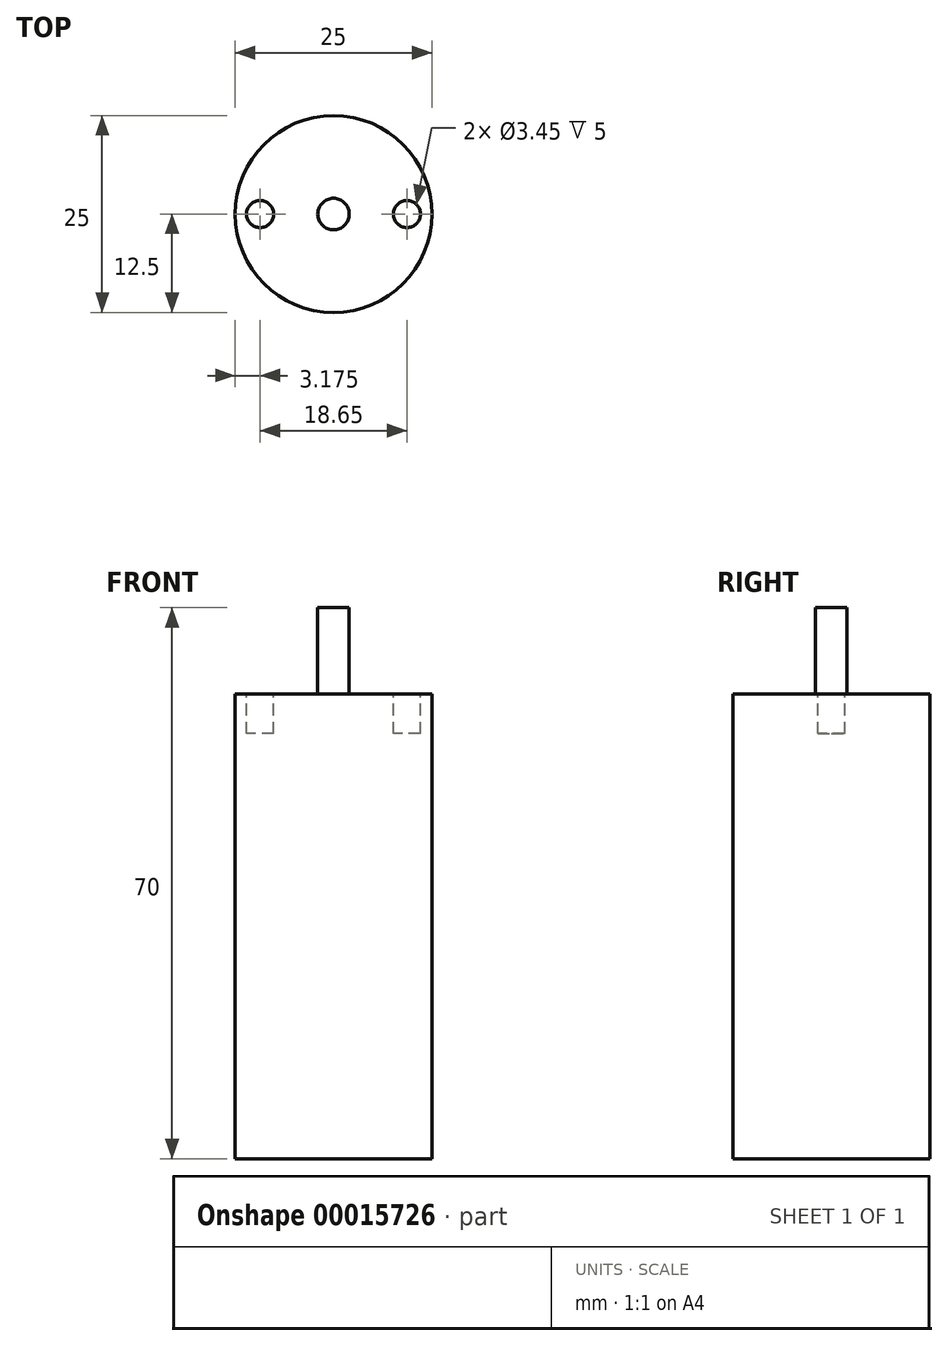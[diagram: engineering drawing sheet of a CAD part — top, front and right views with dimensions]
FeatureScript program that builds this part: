
annotation { "Feature Type Name" : "Feature", "Feature Type Description" : "" }
export const myFeature = defineFeature(function(context is Context, id is Id, definition is map)
    precondition{}
    {
        {
            var Q0;
            Q0=qCreatedBy(makeId("Top.planeOp"),FACE);
            var sketch = newSketch(context, id + "F0", { "sketchPlane" : qUnion([Q0])});
            skCircle(sketch, "E0", {"center": v(0, 0) * mm, "radius": 12.5 * mm});
            skSolve(sketch);
        }
        {
            var Q0;
            Q0=qSketchRegion(id+"F0",true);
            extrude(context, id + "F1", {"entities" : qUnion([Q0]), "depth" : 59 * mm});
        }
        {
            var Q0;
            Q0=makeQuery(id+"F1.opExtrude","CAP_FACE",FACE,{"disambiguationData":[OSD([sQuery(id+"F0.wireOp",EDGE,"E0")])],"isStart":false});
            var sketch = newSketch(context, id + "F2", { "sketchPlane" : qUnion([Q0])});
            skCircle(sketch, "E1", {"center": v(0, 0) * mm, "radius": 2 * mm});
            skSolve(sketch);
        }
        {
            var Q0;
            Q0=qSketchRegion(id+"F2",true);
            extrude(context, id + "F3", {"entities" : qUnion([Q0]), "operationType" : NewBodyOperationType.ADD, "depth" : 11 * mm});
        }
        {
            var Q0;
            Q0=makeQuery(id+"F1.opExtrude","CAP_FACE",FACE,{"disambiguationData":[OSD([sQuery(id+"F0.wireOp",EDGE,"E0")])],"isStart":false});
            var sketch = newSketch(context, id + "F4", { "sketchPlane" : qUnion([Q0])});
            skLineSegment(sketch, "E2", {"start": v(-9.33, 0) * mm, "end": v(9.33, 0) * mm, "construction": true});
            skPoint(sketch, "E3", {"position": v(0, 0) * mm});
            skCircle(sketch, "E4", {"center": v(-9.33, 0) * mm, "radius": 1.73 * mm});
            skCircle(sketch, "E5", {"center": v(9.33, 0) * mm, "radius": 1.73 * mm});
            skSolve(sketch);
        }
        {
            var Q0;
            Q0=qSketchRegion(id+"F4",true);
            extrude(context, id + "F5", {"entities" : qUnion([Q0]), "operationType" : NewBodyOperationType.REMOVE, "oppositeDirection" : true, "depth" : 5 * mm});
        }
    });
